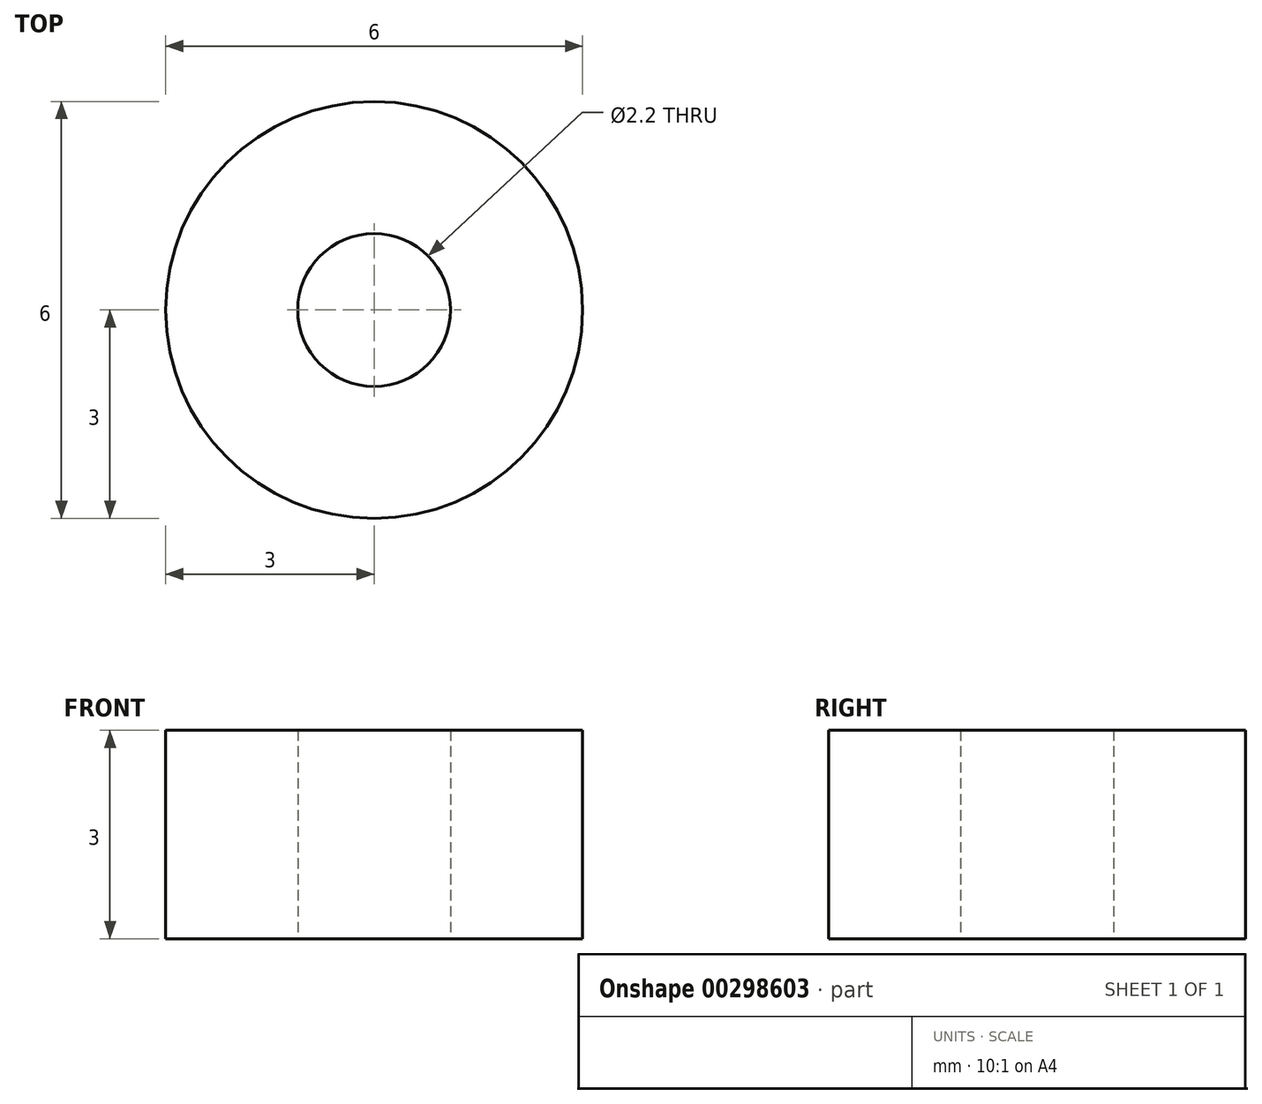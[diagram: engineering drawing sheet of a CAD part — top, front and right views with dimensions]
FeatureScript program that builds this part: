
annotation { "Feature Type Name" : "Feature", "Feature Type Description" : "" }
export const myFeature = defineFeature(function(context is Context, id is Id, definition is map)
    precondition{}
    {
        {
            var Q0;
            Q0=qCreatedBy(makeId("Top.planeOp"),FACE);
            var sketch = newSketch(context, id + "F0", { "sketchPlane" : qUnion([Q0])});
            skCircle(sketch, "E0", {"center": v(0, 0) * mm, "radius": 3 * mm});
            skCircle(sketch, "E1", {"center": v(0, 0) * mm, "radius": 1.1 * mm});
            skSolve(sketch);
        }
        {
            var Q0;
            Q0 = qSketchRegion(id + "F0", true);
            extrude(context, id + "F1", {"entities" : qUnion([Q0]), "depth" : 3 * mm});
        }
    });
